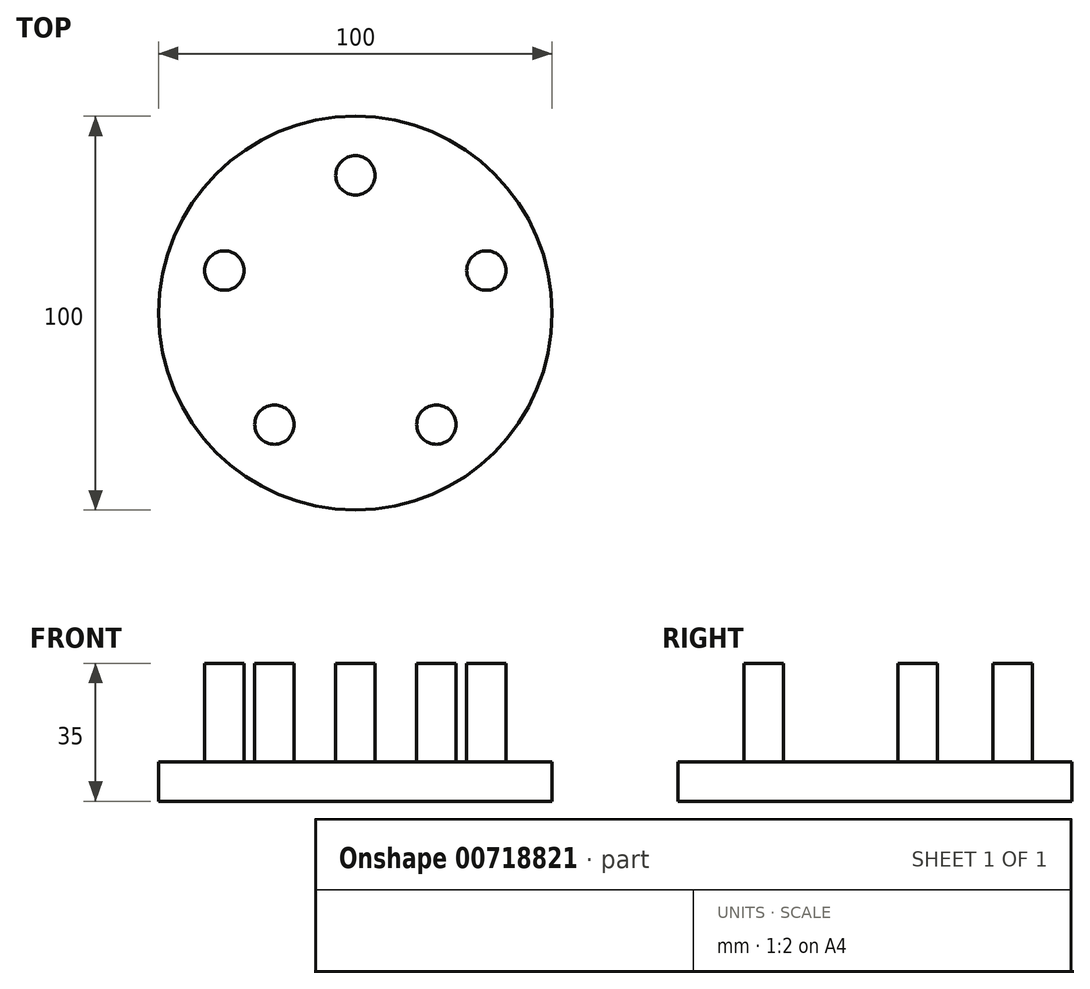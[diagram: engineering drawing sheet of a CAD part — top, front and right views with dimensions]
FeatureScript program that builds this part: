
annotation { "Feature Type Name" : "Feature", "Feature Type Description" : "" }
export const myFeature = defineFeature(function(context is Context, id is Id, definition is map)
    precondition{}
    {
        {
            var Q0;
            Q0=qCreatedBy(makeId("Top.planeOp"),FACE);
            var sketch = newSketch(context, id + "F0", { "sketchPlane" : qUnion([Q0])});
            skCircle(sketch, "E0", {"center": v(0, 0) * mm, "radius": 50 * mm});
            skSolve(sketch);
        }
        {
            var Q0;
            Q0=makeQuery(id+"F0.imprint","IMPRINT",FACE,{"disambiguationData":[TD([[makeQuery(id+"F0.imprint","IMPRINT",EDGE,{"derivedFrom":sQuery(id+"F0.wireOp",EDGE,"E0")}),1.0]])]});
            var Q1;
            Q1=sQuery(id+"F0.wireOp",EDGE,"E0");
            extrude(context, id + "F1", {"entities" : qUnion([Q0]), "surfaceEntities" : qUnion([Q1]), "endBound" : BoundingType.SYMMETRIC, "depth" : 10 * mm, "offsetDistance" : 25 * mm});
        }
        {
            var Q0;
            Q0=makeQuery(id+"F1.opExtrude","CAP_FACE",FACE,{"disambiguationData":[OSD([sQuery(id+"F0.wireOp",EDGE,"E0")])],"isStart":false});
            var sketch = newSketch(context, id + "F2", { "sketchPlane" : qUnion([Q0])});
            skCircle(sketch, "E1", {"center": v(0, 35) * mm, "radius": 5 * mm});
            skPoint(sketch, "E2.center", {"position": v(0, 0) * mm});
            skLineSegment(sketch, "E2.anchor1", {"start": v(0, 0) * mm, "end": v(0, 35) * mm, "construction": true});
            skLineSegment(sketch, "E2.anchor2", {"start": v(0, 0) * mm, "end": v(0, 35) * mm, "construction": true});
            skCircle(sketch, "E3.1.0", {"center": v(-33.29, 10.82) * mm, "radius": 5 * mm});
            skCircle(sketch, "E3.2.0", {"center": v(-20.57, -28.32) * mm, "radius": 5 * mm});
            skCircle(sketch, "E4.1.3.0", {"center": v(20.57, -28.32) * mm, "radius": 5 * mm});
            skCircle(sketch, "E5.1.4.0", {"center": v(33.29, 10.82) * mm, "radius": 5 * mm});
            skSolve(sketch);
        }
        {
            var Q0;
            Q0 = qSketchRegion(id + "F2", true);
            var Q1;
            Q1=sQuery(id+"F2.wireOp",EDGE,"E1");
            extrude(context, id + "F3", {"entities" : qUnion([Q0]), "surfaceEntities" : qUnion([Q1]), "depth" : 25 * mm, "offsetDistance" : 25 * mm});
        }
    });
